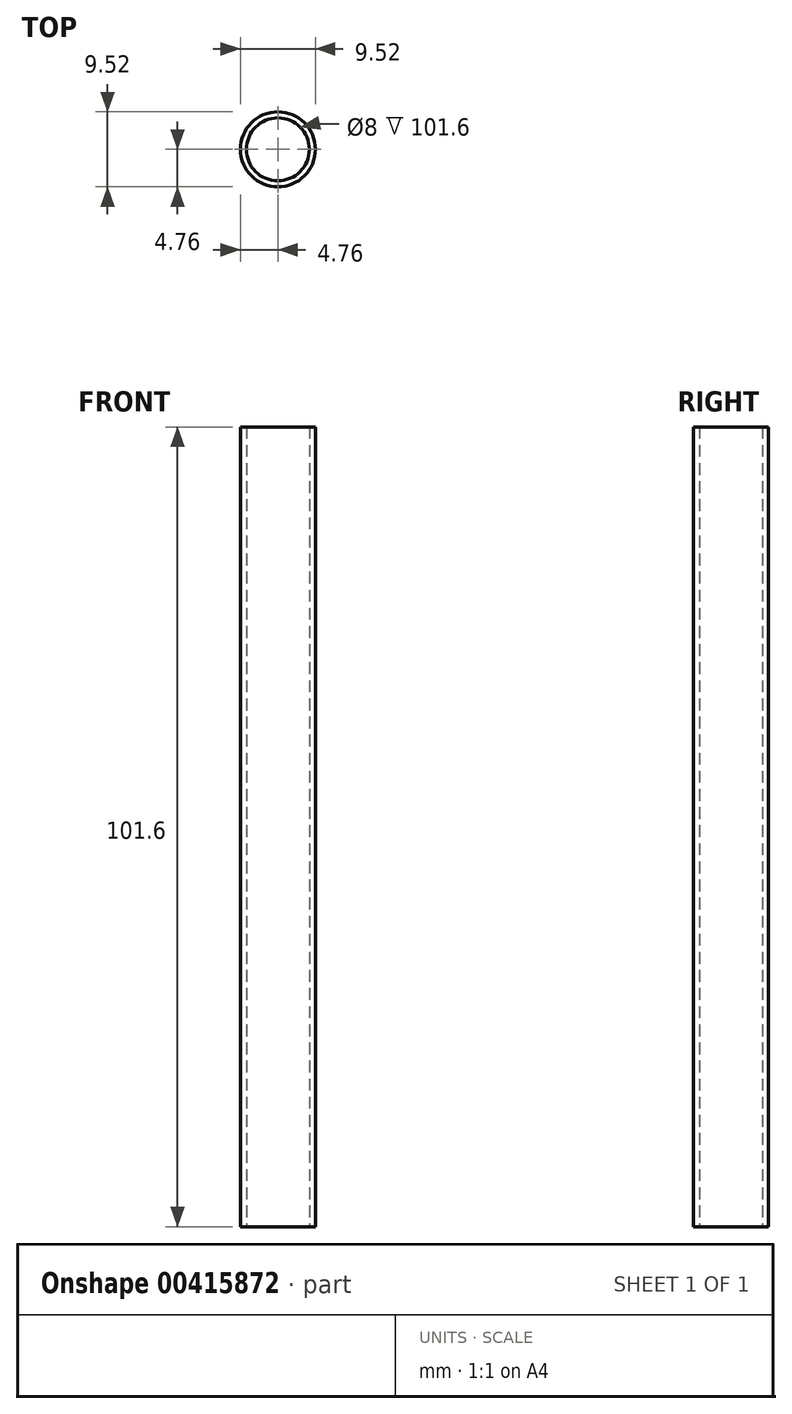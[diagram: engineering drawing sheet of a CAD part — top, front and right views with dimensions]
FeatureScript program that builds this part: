
annotation { "Feature Type Name" : "Feature", "Feature Type Description" : "" }
export const myFeature = defineFeature(function(context is Context, id is Id, definition is map)
    precondition{}
    {
        {
            var Q0;
            Q0=qCreatedBy(makeId("Top.planeOp"),FACE);
            var sketch = newSketch(context, id + "F0", { "sketchPlane" : qUnion([Q0])});
            skCircle(sketch, "E0", {"center": v(0, 0) * mm, "radius": 4.76 * mm});
            skCircle(sketch, "E1.0", {"center": v(0, 0) * mm, "radius": 4 * mm});
            skSolve(sketch);
        }
        {
            var Q0;
            Q0=qSketchRegion(id+"F0",true);
            extrude(context, id + "F1", {"entities" : qUnion([Q0]), "depth" : 101.6 * mm});
        }
    });
